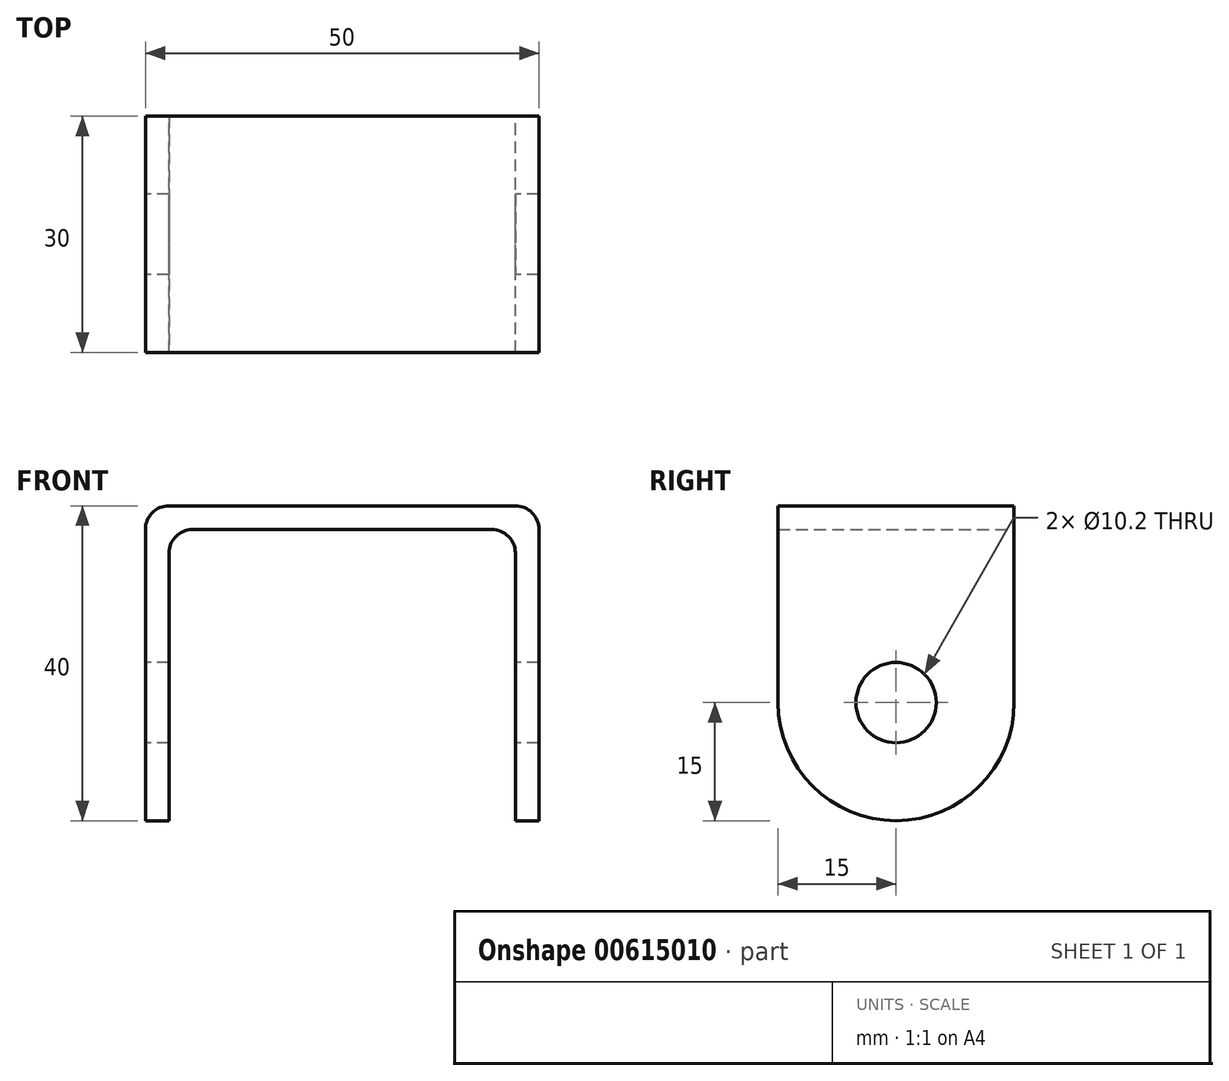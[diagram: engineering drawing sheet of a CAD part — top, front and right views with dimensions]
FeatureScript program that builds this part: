
annotation { "Feature Type Name" : "Feature", "Feature Type Description" : "" }
export const myFeature = defineFeature(function(context is Context, id is Id, definition is map)
    precondition{}
    {
        {
            var Q0;
            Q0=qCreatedBy(makeId("Front.planeOp"),FACE);
            var sketch = newSketch(context, id + "F0", { "sketchPlane" : qUnion([Q0])});
            skLineSegment(sketch, "E0", {"start": v(0, 0) * mm, "end": v(0, 37) * mm});
            skLineSegment(sketch, "E1", {"start": v(0, 37) * mm, "end": v(44, 37) * mm});
            skLineSegment(sketch, "E2", {"start": v(44, 37) * mm, "end": v(44, 0) * mm});
            skLineSegment(sketch, "E3.0", {"start": v(47, 40) * mm, "end": v(47, 0) * mm});
            skLineSegment(sketch, "E3.1", {"start": v(-3, 40) * mm, "end": v(47, 40) * mm});
            skLineSegment(sketch, "E3.2", {"start": v(-3, 0) * mm, "end": v(-3, 40) * mm});
            skLineSegment(sketch, "E4", {"start": v(0, 0) * mm, "end": v(-3, 0) * mm});
            skLineSegment(sketch, "E5", {"start": v(47, 0) * mm, "end": v(44, 0) * mm});
            skSolve(sketch);
        }
        {
            var Q0;
            Q0 = qSketchRegion(id + "F0", true);
            extrude(context, id + "F1", {"entities" : qUnion([Q0]), "depth" : 30 * mm, "offsetDistance" : 25 * mm});
        }
        {
            var Q0;
            Q0=makeQuery(id+"F1.opExtrude","SWEPT_FACE",FACE,{"disambiguationData":[OSD([sQuery(id+"F0.wireOp",EDGE,"E3.2")])]});
            var sketch = newSketch(context, id + "F2", { "sketchPlane" : qUnion([Q0])});
            skCircle(sketch, "E6", {"center": v(15, 15) * mm, "radius": 5.1 * mm});
            skSolve(sketch);
        }
        {
            var Q0;
            Q0 = qSketchRegion(id + "F2", true);
            extrude(context, id + "F3", {"entities" : qUnion([Q0]), "operationType" : NewBodyOperationType.REMOVE, "endBound" : BoundingType.THROUGH_ALL, "oppositeDirection" : true, "depth" : 25 * mm, "offsetDistance" : 25 * mm});
        }
        {
            var Q0;
            Q0=makeQuery(id+"F1.opExtrude","CAP_EDGE",EDGE,{"disambiguationData":[OSD([sQuery(id+"F0.wireOp",EDGE,"E5")])],"isStart":true});
            var Q1;
            Q1=makeQuery(id+"F1.opExtrude","CAP_EDGE",EDGE,{"disambiguationData":[OSD([sQuery(id+"F0.wireOp",EDGE,"E5")])],"isStart":false});
            var Q2;
            Q2=makeQuery(id+"F1.opExtrude","CAP_EDGE",EDGE,{"disambiguationData":[OSD([sQuery(id+"F0.wireOp",EDGE,"E4")])],"isStart":false});
            var Q3;
            Q3=makeQuery(id+"F1.opExtrude","CAP_EDGE",EDGE,{"disambiguationData":[OSD([sQuery(id+"F0.wireOp",EDGE,"E4")])],"isStart":true});
            fillet(context, id + "F4", {"entities" : qUnion([Q0, Q1, Q2, Q3]), "radius" : 15 * mm, "tangentPropagation" : true, "allowEdgeOverflow" : false});
        }
        {
            var Q0;
            Q0=makeQuery(id+"F1.opExtrude","SWEPT_EDGE",EDGE,{"disambiguationData":[OSD([sQuery(id+"F0.wireOp",EDGE,"E0"),sQuery(id+"F0.wireOp",EDGE,"E1")])]});
            var Q1;
            Q1=makeQuery(id+"F1.opExtrude","SWEPT_EDGE",EDGE,{"disambiguationData":[OSD([sQuery(id+"F0.wireOp",EDGE,"E1"),sQuery(id+"F0.wireOp",EDGE,"E2")])]});
            var Q2;
            Q2=makeQuery(id+"F1.opExtrude","SWEPT_EDGE",EDGE,{"disambiguationData":[OSD([sQuery(id+"F0.wireOp",EDGE,"E3.0"),sQuery(id+"F0.wireOp",EDGE,"E3.1")])]});
            var Q3;
            Q3=makeQuery(id+"F1.opExtrude","SWEPT_EDGE",EDGE,{"disambiguationData":[OSD([sQuery(id+"F0.wireOp",EDGE,"E3.1"),sQuery(id+"F0.wireOp",EDGE,"E3.2")])]});
            fillet(context, id + "F5", {"entities" : qUnion([Q0, Q1, Q2, Q3]), "radius" : 3 * mm, "tangentPropagation" : true, "allowEdgeOverflow" : false});
        }
    });
